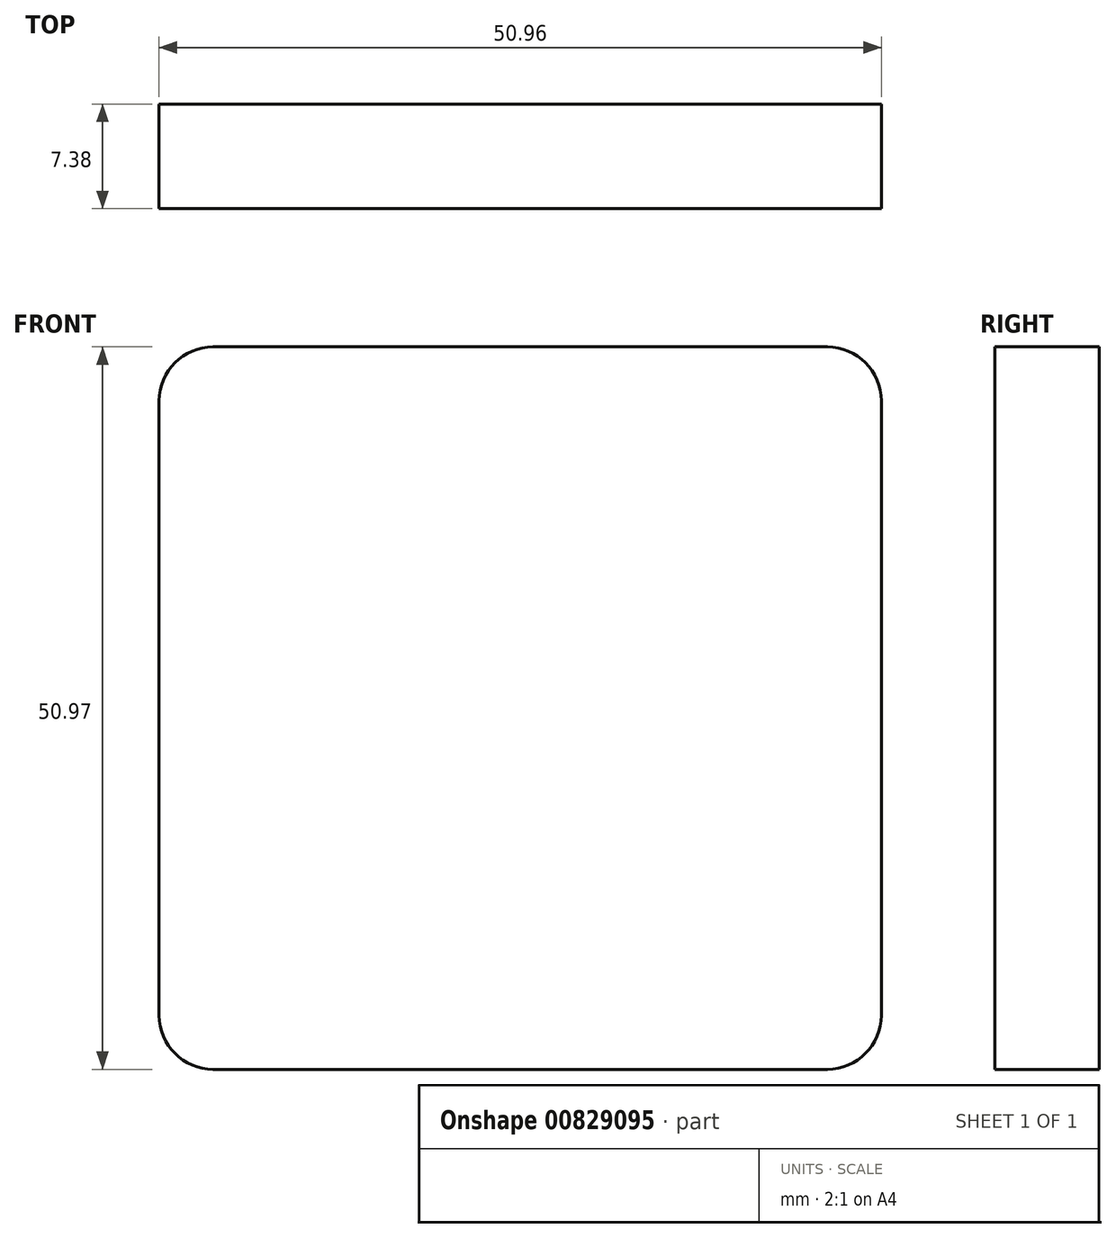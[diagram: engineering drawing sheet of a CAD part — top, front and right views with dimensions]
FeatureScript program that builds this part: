
annotation { "Feature Type Name" : "Feature", "Feature Type Description" : "" }
export const myFeature = defineFeature(function(context is Context, id is Id, definition is map)
    precondition{}
    {
        {
            var Q0;
            Q0=qCreatedBy(makeId("Front.planeOp"),FACE);
            var sketch = newSketch(context, id + "F0", { "sketchPlane" : qUnion([Q0])});
            skLineSegment(sketch, "E0", {"start": v(-25.48, 0) * mm, "end": v(-25.48, -50.97) * mm});
            skLineSegment(sketch, "E1", {"start": v(-25.48, 0) * mm, "end": v(25.48, 0) * mm});
            skLineSegment(sketch, "E2", {"start": v(25.48, 0) * mm, "end": v(25.48, -50.97) * mm});
            skLineSegment(sketch, "E3", {"start": v(-25.48, -50.97) * mm, "end": v(25.48, -50.97) * mm});
            skLineSegment(sketch, "E4", {"start": v(0, 30.55) * mm, "end": v(0, -39.32) * mm, "construction": true});
            skSolve(sketch);
        }
        {
            var Q0;
            Q0=makeQuery(id+"F0.imprint","IMPRINT",FACE,{"disambiguationData":[TD([[makeQuery(id+"F0.imprint","IMPRINT",EDGE,{"derivedFrom":sQuery(id+"F0.wireOp",EDGE,"E0")}),1.0]])]});
            extrude(context, id + "F1", {"entities" : qUnion([Q0]), "depth" : 7.38 * mm, "offsetDistance" : 25.4 * mm});
        }
        {
            var Q0;
            Q0=makeQuery(id+"F1.opExtrude","SWEPT_EDGE",EDGE,{"disambiguationData":[OSD([sQuery(id+"F0.wireOp",EDGE,"E1"),sQuery(id+"F0.wireOp",EDGE,"E2")])]});
            var Q1;
            Q1=makeQuery(id+"F1.opExtrude","SWEPT_EDGE",EDGE,{"disambiguationData":[OSD([sQuery(id+"F0.wireOp",EDGE,"E0"),sQuery(id+"F0.wireOp",EDGE,"E1")])]});
            var Q2;
            Q2=makeQuery(id+"F1.opExtrude","SWEPT_EDGE",EDGE,{"disambiguationData":[OSD([sQuery(id+"F0.wireOp",EDGE,"E2"),sQuery(id+"F0.wireOp",EDGE,"E3")])]});
            var Q3;
            Q3=makeQuery(id+"F1.opExtrude","SWEPT_EDGE",EDGE,{"disambiguationData":[OSD([sQuery(id+"F0.wireOp",EDGE,"E0"),sQuery(id+"F0.wireOp",EDGE,"E3")])]});
            fillet(context, id + "F2", {"entities" : qUnion([Q0, Q1, Q2, Q3]), "radius" : 3.8 * mm, "tangentPropagation" : true, "allowEdgeOverflow" : false});
        }
    });
